# Revit family: Anti-climb Device
name_source: partatom
category: Generic Models
units: mm (PartAtom-declared; Revit-internal decimal feet)

## family parameters
Always vertical = Yes
Can host rebar = No
Cut with Voids When Loaded = No
Maintain Annotation Orientation = No
Part Type = Normal
Room Calculation Point = No
Round Connector Dimension = Use Diameter
Shared = No
Work Plane-Based = No

## types (1)
- Anti-climb Device
    Default Elevation = 0 mm  [stored 0 ft]
    Height = 734 mm
    Length = 720 mm
    Outer Lower Decking Width = 0 mm  [stored 0 ft]
    Taper Angle = 22.24°
    Vertical Distance between floor and lower end = 0 mm  [stored 0 ft]
    Vertical Distance between handrail and access restriction device = 0 mm  [stored 0 ft]
    Width = 250 mm

note: [stored X ft] marks values corroborated as IEEE doubles in the binary element streams (Revit-internal decimal feet)

## geometry (parser evidence)
native form markers: Sweep x3
no freeform markers — native parametric forms only
